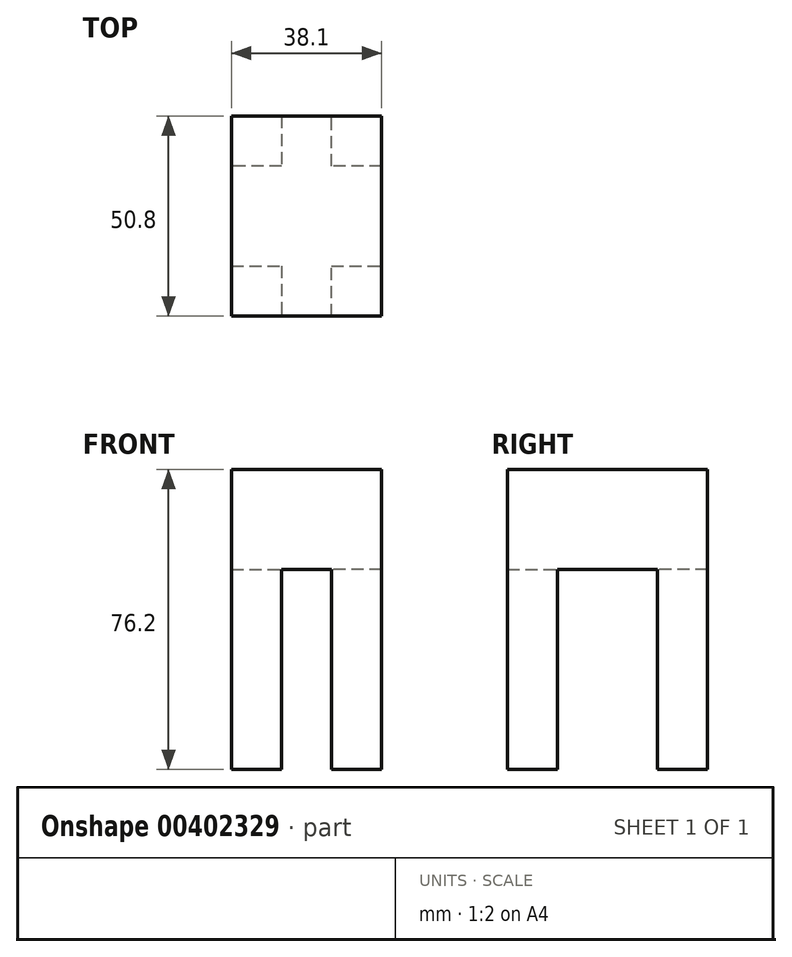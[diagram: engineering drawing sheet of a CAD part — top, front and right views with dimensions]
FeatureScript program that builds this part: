
annotation { "Feature Type Name" : "Feature", "Feature Type Description" : "" }
export const myFeature = defineFeature(function(context is Context, id is Id, definition is map)
    precondition{}
    {
        {
            var Q0;
            Q0=qCreatedBy(makeId("Top.planeOp"),FACE);
            var sketch = newSketch(context, id + "F0", { "sketchPlane" : qUnion([Q0])});
            skLineSegment(sketch, "E0.bottom", {"start": v(-19.05, 25.4) * mm, "end": v(19.05, 25.4) * mm});
            skLineSegment(sketch, "E0.top", {"start": v(-19.05, -25.4) * mm, "end": v(19.05, -25.4) * mm});
            skLineSegment(sketch, "E0.left", {"start": v(-19.05, 25.4) * mm, "end": v(-19.05, -25.4) * mm});
            skLineSegment(sketch, "E0.right", {"start": v(19.05, 25.4) * mm, "end": v(19.05, -25.4) * mm});
            skPoint(sketch, "E0.middle", {"position": v(0, 0) * mm});
            skSolve(sketch);
        }
        {
            var Q0;
            Q0=qSketchRegion(id+"F0",true);
            extrude(context, id + "F1", {"entities" : qUnion([Q0]), "depth" : 76.2 * mm, "symmetric" : true});
        }
        {
            var Q0;
            Q0=makeQuery(id+"F1.opExtrude","CAP_FACE",FACE,{"disambiguationData":[OSD([sQuery(id+"F0.wireOp",EDGE,"E0.bottom"),sQuery(id+"F0.wireOp",EDGE,"E0.top"),sQuery(id+"F0.wireOp",EDGE,"E0.left"),sQuery(id+"F0.wireOp",EDGE,"E0.right")])],"isStart":true});
            var sketch = newSketch(context, id + "F2", { "sketchPlane" : qUnion([Q0])});
            skLineSegment(sketch, "E1", {"start": v(-6.35, 25.4) * mm, "end": v(6.35, 25.4) * mm});
            skLineSegment(sketch, "E2", {"start": v(6.35, 25.4) * mm, "end": v(6.35, 12.7) * mm});
            skLineSegment(sketch, "E3", {"start": v(6.35, 12.7) * mm, "end": v(19.05, 12.7) * mm});
            skLineSegment(sketch, "E4", {"start": v(19.05, 12.7) * mm, "end": v(19.05, -12.7) * mm});
            skLineSegment(sketch, "E5", {"start": v(19.05, -12.7) * mm, "end": v(6.35, -12.7) * mm});
            skLineSegment(sketch, "E6", {"start": v(6.35, -12.7) * mm, "end": v(6.35, -25.4) * mm});
            skLineSegment(sketch, "E7", {"start": v(6.35, -25.4) * mm, "end": v(-6.35, -25.4) * mm});
            skLineSegment(sketch, "E8", {"start": v(-6.35, -25.4) * mm, "end": v(-6.35, -12.7) * mm});
            skLineSegment(sketch, "E9", {"start": v(-6.35, -12.7) * mm, "end": v(-19.05, -12.7) * mm});
            skLineSegment(sketch, "E10", {"start": v(-19.05, -12.7) * mm, "end": v(-19.05, 12.7) * mm});
            skLineSegment(sketch, "E11", {"start": v(-19.05, 12.7) * mm, "end": v(-6.35, 12.7) * mm});
            skLineSegment(sketch, "E12", {"start": v(-6.35, 12.7) * mm, "end": v(-6.35, 25.4) * mm});
            skSolve(sketch);
        }
        {
            var Q0;
            Q0=qSketchRegion(id+"F2",true);
            extrude(context, id + "F3", {"entities" : qUnion([Q0]), "operationType" : NewBodyOperationType.REMOVE, "oppositeDirection" : true, "depth" : 50.8 * mm});
        }
    });
